# Revit family: HL_RU_Roof drain_HL64HSafe-B-221103
name_source: partatom
category: Sanitärinstallationen
units: mm (PartAtom-declared; Revit-internal decimal feet)

## family parameters
Arbeitsebenenbasiert = Nein
Beim Laden mit Abzugskörper schneiden = Nein
Bemaßung runder Anschluss = Durchmesser verwenden
Gemeinsam genutzt = Nein
Immer vertikal = Ja
OmniClass-Nummer = 23.70.50.21.24.14
OmniClass-Titel = Deck Waste Water Drains
Raumberechnungspunkt = Ja
Teiletyp = Normal

## types (1)
- HL_Кровельная воронка_HL64HSafe
    Abwasserrohrverbindung = Ja
    Bauelement = HL64HSafe
    Beschreibung = Кровельные воронки
    EAN = 9003076040919
    HW-Verbindung = Nein
    Hersteller = HL Hutterer & Lechner GmbH
    KW-Verbindung = Nein
    Lüftungsverbindung = Nein
    Modell = HL64HSafe
    Typenkommentare = HL64HSafe, Воронка для аварийного водостока с горизонтальным выпуском DN75/110 с полимербитумным полотном, с возможностью регулировки толщины слоя воды
    URL = http://www.hutterer-lechner.com
    Vorgabe-Ansicht = 0 mm  [stored 0 ft]
    ВЕС = 3,254 [kg]
    ВЫСОТА МОНТАЖА = 150mm
    МАТЕРИАЛ = PP
    РАЗМЕР = DN75/110
    РЕШЁТКА = Laubfangkorb d 262 mm

note: [stored X ft] marks values corroborated as IEEE doubles in the binary element streams (Revit-internal decimal feet)

## geometry (parser evidence)
native form markers: Sweep x5
no freeform markers — native parametric forms only
